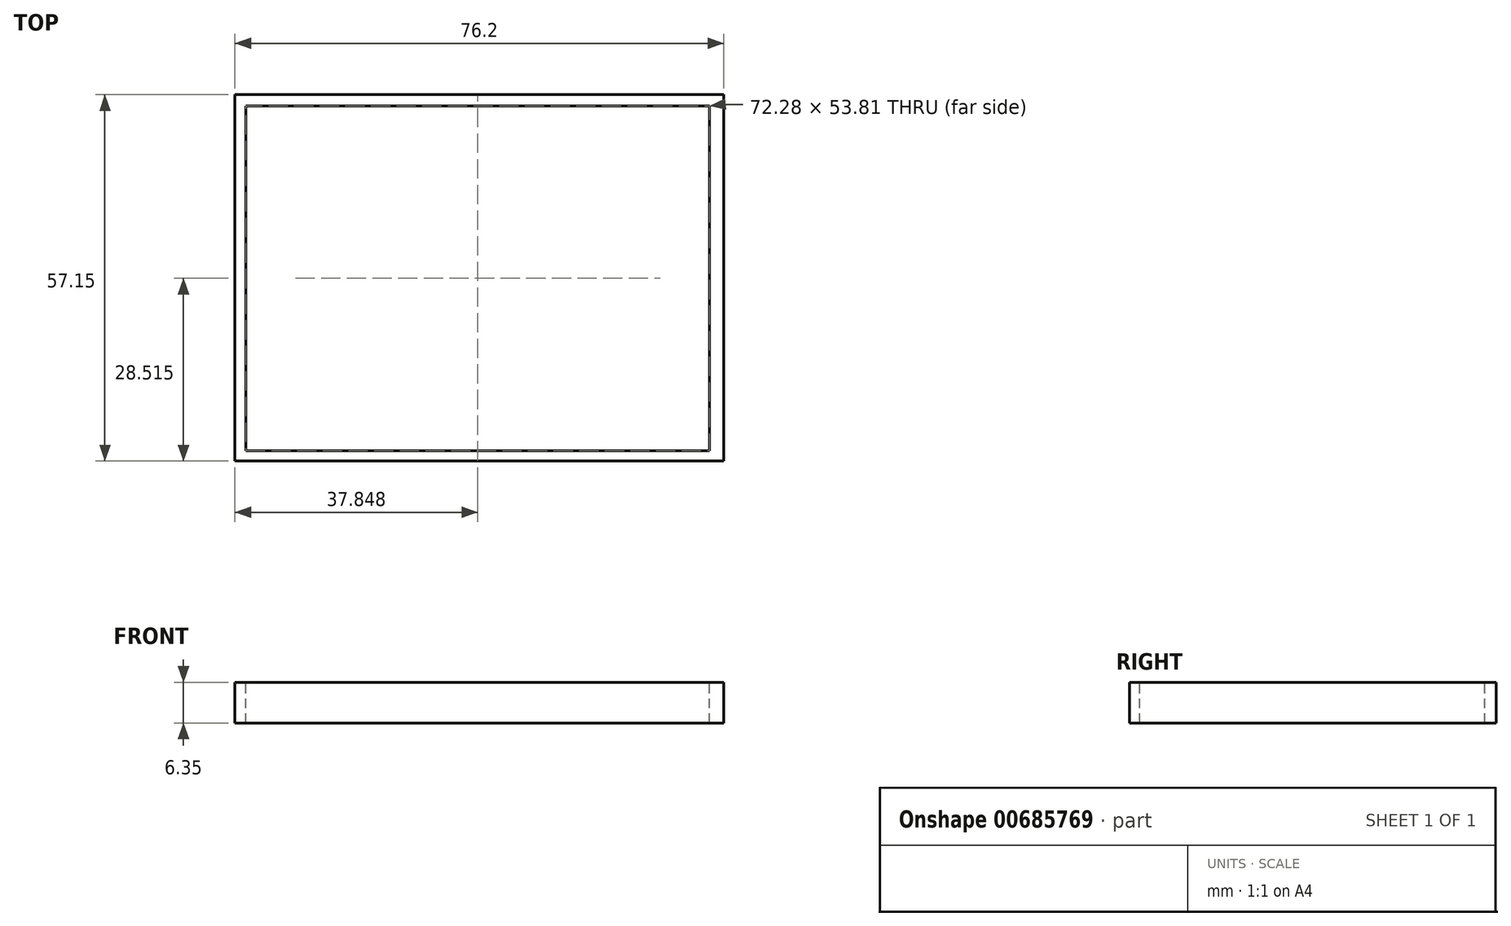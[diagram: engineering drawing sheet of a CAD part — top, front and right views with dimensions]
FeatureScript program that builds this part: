
annotation { "Feature Type Name" : "Feature", "Feature Type Description" : "" }
export const myFeature = defineFeature(function(context is Context, id is Id, definition is map)
    precondition{}
    {
        {
            var Q0;
            Q0=qCreatedBy(makeId("Top.planeOp"),FACE);
            var sketch = newSketch(context, id + "F0", { "sketchPlane" : qUnion([Q0])});
            skLineSegment(sketch, "E0.bottom", {"start": v(-28.11, 22.21) * mm, "end": v(48.09, 22.21) * mm});
            skLineSegment(sketch, "E0.top", {"start": v(-28.11, -34.94) * mm, "end": v(48.09, -34.94) * mm});
            skLineSegment(sketch, "E0.left", {"start": v(-28.11, 22.21) * mm, "end": v(-28.11, -34.94) * mm});
            skLineSegment(sketch, "E0.right", {"start": v(48.09, 22.21) * mm, "end": v(48.09, -34.94) * mm});
            skSolve(sketch);
        }
        {
            var Q0;
            Q0=makeQuery(id+"F0.imprint","IMPRINT",FACE,{"disambiguationData":[TD([[makeQuery(id+"F0.imprint","IMPRINT",EDGE,{"derivedFrom":sQuery(id+"F0.wireOp",EDGE,"E0.bottom")}),-1.0]])]});
            extrude(context, id + "F1", {"entities" : qUnion([Q0]), "endBound" : BoundingType.SYMMETRIC, "depth" : 6.35 * mm, "offsetDistance" : 25.4 * mm});
        }
        {
            var Q0;
            Q0=makeQuery(id+"F1.opExtrude","CAP_FACE",FACE,{"disambiguationData":[OSD([sQuery(id+"F0.wireOp",EDGE,"E0.bottom"),sQuery(id+"F0.wireOp",EDGE,"E0.top"),sQuery(id+"F0.wireOp",EDGE,"E0.left"),sQuery(id+"F0.wireOp",EDGE,"E0.right")])],"isStart":false});
            var sketch = newSketch(context, id + "F2", { "sketchPlane" : qUnion([Q0])});
            skLineSegment(sketch, "E1.bottom", {"start": v(-26.4, 20.48) * mm, "end": v(45.88, 20.48) * mm});
            skLineSegment(sketch, "E1.top", {"start": v(-26.4, -33.33) * mm, "end": v(45.88, -33.33) * mm});
            skLineSegment(sketch, "E1.left", {"start": v(-26.4, 20.48) * mm, "end": v(-26.4, -33.33) * mm});
            skLineSegment(sketch, "E1.right", {"start": v(45.88, 20.48) * mm, "end": v(45.88, -33.33) * mm});
            skSolve(sketch);
        }
        {
            var Q0;
            Q0 = qSketchRegion(id + "F2", true);
            extrude(context, id + "F3", {"entities" : qUnion([Q0]), "operationType" : NewBodyOperationType.REMOVE, "endBound" : BoundingType.UP_TO_NEXT, "oppositeDirection" : true, "depth" : 25.4 * mm, "offsetDistance" : 25.4 * mm});
        }
    });
